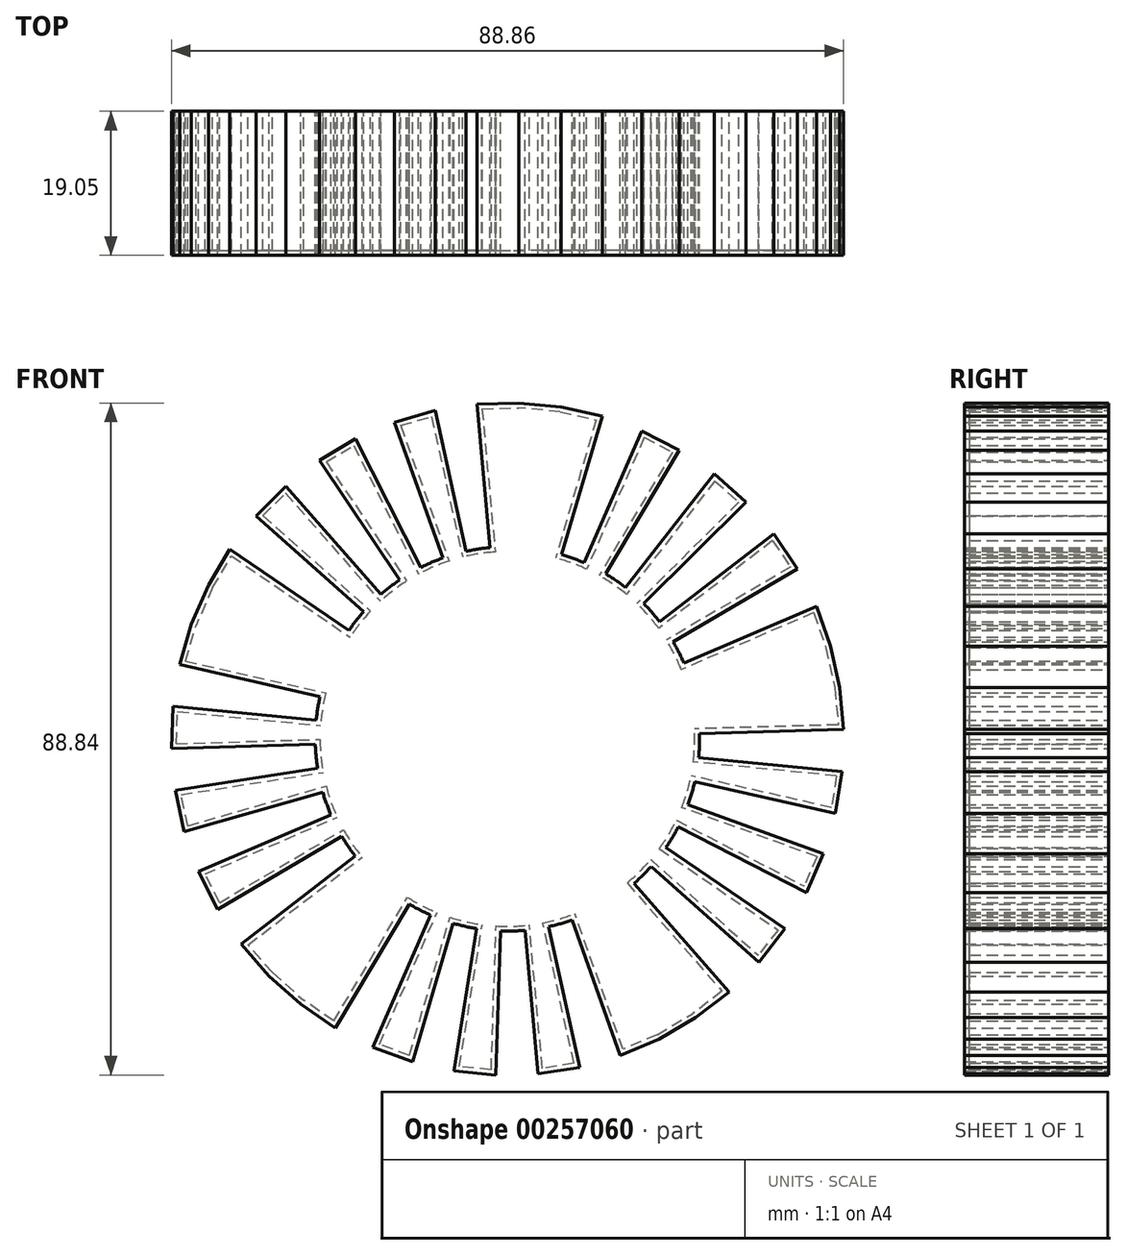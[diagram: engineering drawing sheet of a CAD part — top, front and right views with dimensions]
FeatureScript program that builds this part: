
annotation { "Feature Type Name" : "Feature", "Feature Type Description" : "" }
export const myFeature = defineFeature(function(context is Context, id is Id, definition is map)
    precondition{}
    {
        {
            var Q0;
            Q0=qCreatedBy(makeId("Front.planeOp"),FACE);
            var sketch = newSketch(context, id + "F0", { "sketchPlane" : qUnion([Q0])});
            skArc(sketch, "E0.cCircle", {"start": v(-9.56, 43.4) * mm, "mid": v(-12.27, 42.72) * mm, "end": v(-14.93, 41.87) * mm, "construction": true});
            skLineSegment(sketch, "E0.1", {"start": v(40.85, 17.53) * mm, "end": v(42.72, 12.27) * mm});
            skLineSegment(sketch, "E0.3", {"start": v(43.92, 6.82) * mm, "end": v(44.43, 1.26) * mm});
            skLineSegment(sketch, "E0.5", {"start": v(44.24, -4.32) * mm, "end": v(43.35, -9.83) * mm});
            skLineSegment(sketch, "E0.7", {"start": v(41.78, -15.18) * mm, "end": v(39.54, -20.3) * mm});
            skLineSegment(sketch, "E0.9", {"start": v(36.69, -25.1) * mm, "end": v(33.25, -29.5) * mm});
            skLineSegment(sketch, "E0.11", {"start": v(29.3, -33.43) * mm, "end": v(24.87, -36.84) * mm});
            skLineSegment(sketch, "E0.13", {"start": v(20.06, -39.67) * mm, "end": v(14.93, -41.87) * mm});
            skLineSegment(sketch, "E0.15", {"start": v(9.56, -43.4) * mm, "end": v(4.05, -44.27) * mm});
            skLineSegment(sketch, "E0.17", {"start": v(-1.53, -44.42) * mm, "end": v(-7.09, -43.88) * mm});
            skLineSegment(sketch, "E0.19", {"start": v(-12.53, -42.65) * mm, "end": v(-17.78, -40.74) * mm});
            skLineSegment(sketch, "E0.21", {"start": v(-22.74, -38.2) * mm, "end": v(-27.35, -35.04) * mm});
            skLineSegment(sketch, "E0.23", {"start": v(-31.53, -31.33) * mm, "end": v(-35.2, -27.14) * mm});
            skLineSegment(sketch, "E0.25", {"start": v(-38.33, -22.5) * mm, "end": v(-40.85, -17.53) * mm});
            skLineSegment(sketch, "E0.27", {"start": v(-42.72, -12.27) * mm, "end": v(-43.92, -6.82) * mm});
            skLineSegment(sketch, "E0.29", {"start": v(-44.43, -1.26) * mm, "end": v(-44.24, 4.32) * mm});
            skLineSegment(sketch, "E0.31", {"start": v(-43.35, 9.83) * mm, "end": v(-41.78, 15.18) * mm});
            skLineSegment(sketch, "E0.33", {"start": v(-39.54, 20.3) * mm, "end": v(-36.69, 25.1) * mm});
            skLineSegment(sketch, "E0.35", {"start": v(-33.25, 29.5) * mm, "end": v(-29.3, 33.43) * mm});
            skLineSegment(sketch, "E0.37", {"start": v(-24.87, 36.84) * mm, "end": v(-20.06, 39.67) * mm});
            skLineSegment(sketch, "E0.39", {"start": v(-14.93, 41.87) * mm, "end": v(-9.56, 43.4) * mm});
            skLineSegment(sketch, "E0.41", {"start": v(-4.05, 44.27) * mm, "end": v(1.53, 44.42) * mm});
            skLineSegment(sketch, "E0.43", {"start": v(7.09, 43.88) * mm, "end": v(12.53, 42.65) * mm});
            skLineSegment(sketch, "E0.45", {"start": v(17.78, 40.74) * mm, "end": v(22.74, 38.2) * mm});
            skLineSegment(sketch, "E0.47", {"start": v(27.35, 35.04) * mm, "end": v(31.53, 31.33) * mm});
            skLineSegment(sketch, "E0.49", {"start": v(35.2, 27.14) * mm, "end": v(38.33, 22.5) * mm});
            skCircle(sketch, "E1", {"center": v(0, 0) * mm, "radius": 25.4 * mm});
            skLineSegment(sketch, "E2", {"start": v(-9.56, 43.4) * mm, "end": v(-5.47, 24.8) * mm});
            skLineSegment(sketch, "E3", {"start": v(-4.05, 44.27) * mm, "end": v(-2.31, 25.3) * mm});
            skLineSegment(sketch, "E4", {"start": v(12.53, 42.65) * mm, "end": v(7.16, 24.37) * mm});
            skLineSegment(sketch, "E5", {"start": v(17.78, 40.74) * mm, "end": v(10.16, 23.28) * mm});
            skLineSegment(sketch, "E6", {"start": v(22.74, 38.2) * mm, "end": v(13, 21.82) * mm});
            skLineSegment(sketch, "E7", {"start": v(27.35, 35.04) * mm, "end": v(15.63, 20.02) * mm});
            skLineSegment(sketch, "E8", {"start": v(31.53, 31.33) * mm, "end": v(18.02, 17.9) * mm});
            skLineSegment(sketch, "E9", {"start": v(35.2, 27.14) * mm, "end": v(20.12, 15.5) * mm});
            skLineSegment(sketch, "E10", {"start": v(38.33, 22.5) * mm, "end": v(21.9, 12.86) * mm});
            skLineSegment(sketch, "E11", {"start": v(40.85, 17.53) * mm, "end": v(23.34, 10.02) * mm});
            skLineSegment(sketch, "E12", {"start": v(44.43, 1.26) * mm, "end": v(25.39, 0.72) * mm});
            skLineSegment(sketch, "E13", {"start": v(44.24, -4.32) * mm, "end": v(25.28, -2.47) * mm});
            skLineSegment(sketch, "E14", {"start": v(43.35, -9.83) * mm, "end": v(24.77, -5.62) * mm});
            skLineSegment(sketch, "E15", {"start": v(41.78, -15.18) * mm, "end": v(23.87, -8.68) * mm});
            skLineSegment(sketch, "E16.MirrorCS", {"start": v(-14.93, 41.87) * mm, "end": v(-8.53, 23.92) * mm});
            skLineSegment(sketch, "E17.MirrorCS", {"start": v(-20.06, 39.67) * mm, "end": v(-11.46, 22.67) * mm});
            skLineSegment(sketch, "E18.MirrorCS", {"start": v(-24.87, 36.84) * mm, "end": v(-14.21, 21.05) * mm});
            skLineSegment(sketch, "E19.MirrorCS", {"start": v(-29.3, 33.43) * mm, "end": v(-16.74, 19.1) * mm});
            skLineSegment(sketch, "E20.MirrorCS", {"start": v(-33.25, 29.5) * mm, "end": v(-19, 16.86) * mm});
            skLineSegment(sketch, "E21.MirrorCS", {"start": v(-36.69, 25.1) * mm, "end": v(-20.96, 14.34) * mm});
            skLineSegment(sketch, "E22.MirrorCS", {"start": v(-43.35, 9.83) * mm, "end": v(-24.77, 5.62) * mm});
            skLineSegment(sketch, "E23.MirrorCS", {"start": v(-44.24, 4.32) * mm, "end": v(-25.28, 2.47) * mm});
            skLineSegment(sketch, "E24.MirrorCS", {"start": v(-44.43, -1.26) * mm, "end": v(-25.39, -0.72) * mm});
            skLineSegment(sketch, "E25.MirrorCS", {"start": v(-43.92, -6.82) * mm, "end": v(-25.1, -3.9) * mm});
            skLineSegment(sketch, "E26.MirrorCS", {"start": v(-42.72, -12.27) * mm, "end": v(-24.41, -7.01) * mm});
            skLineSegment(sketch, "E27.MirrorCS", {"start": v(-40.85, -17.53) * mm, "end": v(-23.34, -10.02) * mm});
            skLineSegment(sketch, "E28.MirrorCS", {"start": v(-38.33, -22.5) * mm, "end": v(-21.9, -12.86) * mm});
            skLineSegment(sketch, "E29.MirrorCS", {"start": v(-35.2, -27.14) * mm, "end": v(-20.12, -15.5) * mm});
            skLineSegment(sketch, "E30", {"start": v(22.6, -11.6) * mm, "end": v(39.54, -20.3) * mm});
            skLineSegment(sketch, "E31", {"start": v(20.96, -14.34) * mm, "end": v(36.69, -25.1) * mm});
            skLineSegment(sketch, "E32", {"start": v(19, -16.86) * mm, "end": v(33.25, -29.5) * mm});
            skLineSegment(sketch, "E33", {"start": v(16.74, -19.1) * mm, "end": v(29.3, -33.43) * mm});
            skLineSegment(sketch, "E34.MirrorCS", {"start": v(9.56, -43.4) * mm, "end": v(5.47, -24.8) * mm});
            skLineSegment(sketch, "E35.MirrorCS", {"start": v(14.93, -41.87) * mm, "end": v(8.53, -23.92) * mm});
            skLineSegment(sketch, "E36.MirrorCS", {"start": v(-22.74, -38.2) * mm, "end": v(-13, -21.82) * mm});
            skLineSegment(sketch, "E37.MirrorCS", {"start": v(-17.78, -40.74) * mm, "end": v(-10.16, -23.28) * mm});
            skLineSegment(sketch, "E38.MirrorCS", {"start": v(-7.09, -43.88) * mm, "end": v(-4.05, -25.08) * mm});
            skLineSegment(sketch, "E39.MirrorCS", {"start": v(-1.53, -44.42) * mm, "end": v(-0.88, -25.38) * mm});
            skPoint(sketch, "E40.MirrorCS.start.orphan", {"position": v(-12.53, -42.65) * mm});
            skPoint(sketch, "E41.MirrorCS.start.orphan", {"position": v(4.05, -44.27) * mm});
            skLineSegment(sketch, "E42", {"start": v(-12.53, -42.65) * mm, "end": v(-7.16, -24.37) * mm});
            skLineSegment(sketch, "E43", {"start": v(4.05, -44.27) * mm, "end": v(2.31, -25.3) * mm});
            skLineSegment(sketch, "E44", {"start": v(42.72, 12.27) * mm, "end": v(43.92, 6.82) * mm});
            skLineSegment(sketch, "E45", {"start": v(7.09, 43.88) * mm, "end": v(1.53, 44.42) * mm});
            skLineSegment(sketch, "E46", {"start": v(-39.54, 20.3) * mm, "end": v(-41.78, 15.18) * mm});
            skLineSegment(sketch, "E47", {"start": v(-31.53, -31.33) * mm, "end": v(-27.35, -35.04) * mm});
            skLineSegment(sketch, "E48", {"start": v(20.06, -39.67) * mm, "end": v(24.87, -36.84) * mm});
            skSolve(sketch);
        }
        {
            var Q0;
            Q0 = qSketchRegion(id + "F0", true);
            extrude(context, id + "F1", {"entities" : qUnion([Q0]), "depth" : 19.05 * mm});
        }
        {
            var Q0;
            Q0=makeQuery(id+"F1.opExtrude","CAP_FACE",FACE,{"disambiguationData":[OSD([sQuery(id+"F0.wireOp",EDGE,"E0.1"),sQuery(id+"F0.wireOp",EDGE,"E0.3"),sQuery(id+"F0.wireOp",EDGE,"E0.5"),sQuery(id+"F0.wireOp",EDGE,"E0.7"),sQuery(id+"F0.wireOp",EDGE,"E0.9"),sQuery(id+"F0.wireOp",EDGE,"E0.11"),sQuery(id+"F0.wireOp",EDGE,"E0.13"),sQuery(id+"F0.wireOp",EDGE,"E0.15"),sQuery(id+"F0.wireOp",EDGE,"E0.17"),sQuery(id+"F0.wireOp",EDGE,"E0.19"),sQuery(id+"F0.wireOp",EDGE,"E0.21"),sQuery(id+"F0.wireOp",EDGE,"E0.23"),sQuery(id+"F0.wireOp",EDGE,"E0.25"),sQuery(id+"F0.wireOp",EDGE,"E0.27"),sQuery(id+"F0.wireOp",EDGE,"E0.29"),sQuery(id+"F0.wireOp",EDGE,"E0.31"),sQuery(id+"F0.wireOp",EDGE,"E0.33"),sQuery(id+"F0.wireOp",EDGE,"E0.35"),sQuery(id+"F0.wireOp",EDGE,"E0.37"),sQuery(id+"F0.wireOp",EDGE,"E0.39"),sQuery(id+"F0.wireOp",EDGE,"E0.41"),sQuery(id+"F0.wireOp",EDGE,"E0.43"),sQuery(id+"F0.wireOp",EDGE,"E0.45"),sQuery(id+"F0.wireOp",EDGE,"E0.47"),sQuery(id+"F0.wireOp",EDGE,"E0.49"),sQuery(id+"F0.wireOp",EDGE,"E1"),sQuery(id+"F0.wireOp",EDGE,"E2"),sQuery(id+"F0.wireOp",EDGE,"E3"),sQuery(id+"F0.wireOp",EDGE,"z1sWIhk1-8U68-gKAl-EIL4-YsX6HyAjruzo"),sQuery(id+"F0.wireOp",EDGE,"goTFUU77-Rhqn-QL9q-NdJa-OHe2fiKNGHK0"),sQuery(id+"F0.wireOp",EDGE,"E4"),sQuery(id+"F0.wireOp",EDGE,"E5"),sQuery(id+"F0.wireOp",EDGE,"E6"),sQuery(id+"F0.wireOp",EDGE,"E7"),sQuery(id+"F0.wireOp",EDGE,"E8"),sQuery(id+"F0.wireOp",EDGE,"E9"),sQuery(id+"F0.wireOp",EDGE,"E10"),sQuery(id+"F0.wireOp",EDGE,"E11"),sQuery(id+"F0.wireOp",EDGE,"aAd8ZC0g-dThq-GAmU-ne6f-NqyACqOZkW08"),sQuery(id+"F0.wireOp",EDGE,"qq479QEf-Kv4v-Tc3t-cECF-8ayoAx7vKxX0"),sQuery(id+"F0.wireOp",EDGE,"E12"),sQuery(id+"F0.wireOp",EDGE,"E13"),sQuery(id+"F0.wireOp",EDGE,"E14"),sQuery(id+"F0.wireOp",EDGE,"E15"),sQuery(id+"F0.wireOp",EDGE,"E16.MirrorCS"),sQuery(id+"F0.wireOp",EDGE,"E17.MirrorCS"),sQuery(id+"F0.wireOp",EDGE,"E18.MirrorCS"),sQuery(id+"F0.wireOp",EDGE,"E19.MirrorCS"),sQuery(id+"F0.wireOp",EDGE,"E20.MirrorCS"),sQuery(id+"F0.wireOp",EDGE,"E21.MirrorCS"),sQuery(id+"F0.wireOp",EDGE,"a47e6d99-0c8e-4f32-bb81-bebe6fd7e0f10.MirrorCS"),sQuery(id+"F0.wireOp",EDGE,"a328149c-aa23-41ce-b25a-3685d72366750.MirrorCS"),sQuery(id+"F0.wireOp",EDGE,"E22.MirrorCS"),sQuery(id+"F0.wireOp",EDGE,"E23.MirrorCS"),sQuery(id+"F0.wireOp",EDGE,"E24.MirrorCS"),sQuery(id+"F0.wireOp",EDGE,"E25.MirrorCS"),sQuery(id+"F0.wireOp",EDGE,"E26.MirrorCS"),sQuery(id+"F0.wireOp",EDGE,"E27.MirrorCS"),sQuery(id+"F0.wireOp",EDGE,"E28.MirrorCS"),sQuery(id+"F0.wireOp",EDGE,"E29.MirrorCS"),sQuery(id+"F0.wireOp",EDGE,"4ac1b494-c149-43da-9a76-13821ffb91700.MirrorCS"),sQuery(id+"F0.wireOp",EDGE,"E30"),sQuery(id+"F0.wireOp",EDGE,"E31"),sQuery(id+"F0.wireOp",EDGE,"E32"),sQuery(id+"F0.wireOp",EDGE,"E33"),sQuery(id+"F0.wireOp",EDGE,"E34.MirrorCS"),sQuery(id+"F0.wireOp",EDGE,"E35.MirrorCS"),sQuery(id+"F0.wireOp",EDGE,"940b54cc-f220-4fc6-a30e-ba0a53f629f30.MirrorCS"),sQuery(id+"F0.wireOp",EDGE,"4e9d13cd-ae0f-4c94-b7b0-f20dd37745fe0.MirrorCS"),sQuery(id+"F0.wireOp",EDGE,"9d5ca4f8-5272-4511-ac9e-2a1458dea17a0.MirrorCS"),sQuery(id+"F0.wireOp",EDGE,"E36.MirrorCS"),sQuery(id+"F0.wireOp",EDGE,"E37.MirrorCS"),sQuery(id+"F0.wireOp",EDGE,"E38.MirrorCS"),sQuery(id+"F0.wireOp",EDGE,"E39.MirrorCS"),sQuery(id+"F0.wireOp",EDGE,"E42"),sQuery(id+"F0.wireOp",EDGE,"E43")])],"isStart":true});
            shell(context, id + "F2", {"entities" : qUnion([Q0]), "thickness" : 0.64 * mm});
        }
    });
